FCSTD DOCUMENT  (FreeCAD 0.18R4 (GitTag))
Label: butelka tył
License: All rights reserved
LicenseURL: http://en.wikipedia.org/wiki/All_rights_reserved
objects: Sketcher::SketchObject×1, PartDesign::Body×1
note: 2 computed .brp shape members not serialized (recipe doc carries the construction recipe); baked Part::Feature solids carry a one-line shape summary decoded from their .brp

FEATURE [Sketcher::SketchObject] Sketch
  MapMode = 5
  Support = -> [XY_Plane]
  sketch-geometry (308):
    g0: LineSegment StartX=0 StartY=0 StartZ=0 EndX=160 EndY=0 EndZ=0
    g1: LineSegment StartX=160 StartY=0 StartZ=0 EndX=160 EndY=17.5 EndZ=0
    g2: LineSegment StartX=160 StartY=17.5 StartZ=0 EndX=156.35 EndY=17.5 EndZ=0
    g3: LineSegment StartX=156.35 StartY=17.5 StartZ=0 EndX=156.35 EndY=20.5 EndZ=0
    g4: LineSegment StartX=156.35 StartY=20.5 StartZ=0 EndX=160 EndY=20.5 EndZ=0
    g5: LineSegment StartX=160 StartY=20.5 StartZ=0 EndX=160 EndY=23.5 EndZ=0
    g6: LineSegment StartX=160 StartY=23.5 StartZ=0 EndX=156.35 EndY=23.5 EndZ=0
    g7: LineSegment StartX=156.35 StartY=23.5 StartZ=0 EndX=156.35 EndY=26.5 EndZ=0
    g8: LineSegment StartX=156.35 StartY=26.5 StartZ=0 EndX=160 EndY=26.5 EndZ=0
    g9: LineSegment StartX=160 StartY=26.5 StartZ=0 EndX=160 EndY=29.5 EndZ=0
    g10: LineSegment StartX=160 StartY=29.5 StartZ=0 EndX=156.35 EndY=29.5 EndZ=0
    g11: LineSegment StartX=156.35 StartY=29.5 StartZ=0 EndX=156.35 EndY=32.5 EndZ=0
    g12: LineSegment StartX=156.35 StartY=32.5 StartZ=0 EndX=160 EndY=32.5 EndZ=0
    g13: LineSegment StartX=160 StartY=32.5 StartZ=0 EndX=160 EndY=35.5 EndZ=0
    g14: LineSegment StartX=160 StartY=35.5 StartZ=0 EndX=156.35 EndY=35.5 EndZ=0
    g15: LineSegment StartX=156.35 StartY=35.5 StartZ=0 EndX=156.35 EndY=38.5 EndZ=0
    g16: LineSegment StartX=156.35 StartY=38.5 StartZ=0 EndX=160 EndY=38.5 EndZ=0
    g17: LineSegment StartX=160 StartY=38.5 StartZ=0 EndX=160 EndY=41.5 EndZ=0
    g18: LineSegment StartX=160 StartY=41.5 StartZ=0 EndX=156.35 EndY=41.5 EndZ=0
    g19: LineSegment StartX=156.35 StartY=41.5 StartZ=0 EndX=156.35 EndY=44.5 EndZ=0
    g20: LineSegment StartX=156.35 StartY=44.5 StartZ=0 EndX=160 EndY=44.5 EndZ=0
    g21: LineSegment StartX=160 StartY=44.5 StartZ=0 EndX=160 EndY=47.5 EndZ=0
    g22: LineSegment StartX=160 StartY=47.5 StartZ=0 EndX=156.35 EndY=47.5 EndZ=0
    g23: LineSegment StartX=156.35 StartY=47.5 StartZ=0 EndX=156.35 EndY=50.5 EndZ=0
    g24: LineSegment StartX=156.35 StartY=50.5 StartZ=0 EndX=160 EndY=50.5 EndZ=0
    g25: LineSegment StartX=160 StartY=50.5 StartZ=0 EndX=160 EndY=53.5 EndZ=0
    g26: LineSegment StartX=160 StartY=53.5 StartZ=0 EndX=156.35 EndY=53.5 EndZ=0
    g27: LineSegment StartX=156.35 StartY=53.5 StartZ=0 EndX=156.35 EndY=56.5 EndZ=0
    g28: LineSegment StartX=156.35 StartY=56.5 StartZ=0 EndX=160 EndY=56.5 EndZ=0
    g29: LineSegment StartX=160 StartY=56.5 StartZ=0 EndX=160 EndY=59.5 EndZ=0
    g30: LineSegment StartX=160 StartY=59.5 StartZ=0 EndX=156.35 EndY=59.5 EndZ=0
    g31: LineSegment StartX=156.35 StartY=59.5 StartZ=0 EndX=156.35 EndY=62.5 EndZ=0
    g32: LineSegment StartX=156.35 StartY=62.5 StartZ=0 EndX=160 EndY=62.5 EndZ=0
    g33: LineSegment StartX=160 StartY=62.5 StartZ=0 EndX=160 EndY=65.5 EndZ=0
    g34: LineSegment StartX=160 StartY=65.5 StartZ=0 EndX=156.35 EndY=65.5 EndZ=0
    g35: LineSegment StartX=156.35 StartY=65.5 StartZ=0 EndX=156.35 EndY=68.5 EndZ=0
    g36: LineSegment StartX=156.35 StartY=68.5 StartZ=0 EndX=160 EndY=68.5 EndZ=0
    g37: LineSegment StartX=160 StartY=68.5 StartZ=0 EndX=160 EndY=71.5 EndZ=0
    g38: LineSegment StartX=160 StartY=71.5 StartZ=0 EndX=156.35 EndY=71.5 EndZ=0
    g39: LineSegment StartX=156.35 StartY=71.5 StartZ=0 EndX=156.35 EndY=74.5 EndZ=0
    g40: LineSegment StartX=156.35 StartY=74.5 StartZ=0 EndX=160 EndY=74.5 EndZ=0
    g41: LineSegment StartX=160 StartY=74.5 StartZ=0 EndX=160 EndY=77.5 EndZ=0
    g42: LineSegment StartX=160 StartY=77.5 StartZ=0 EndX=156.35 EndY=77.5 EndZ=0
    g43: LineSegment StartX=156.35 StartY=77.5 StartZ=0 EndX=156.35 EndY=80.5 EndZ=0
    g44: LineSegment StartX=156.35 StartY=80.5 StartZ=0 EndX=160 EndY=80.5 EndZ=0
    g45: LineSegment StartX=160 StartY=80.5 StartZ=0 EndX=160 EndY=83.5 EndZ=0
    g46: LineSegment StartX=160 StartY=83.5 StartZ=0 EndX=156.35 EndY=83.5 EndZ=0
    g47: LineSegment StartX=156.35 StartY=83.5 StartZ=0 EndX=156.35 EndY=86.5 EndZ=0
    g48: LineSegment StartX=156.35 StartY=86.5 StartZ=0 EndX=160 EndY=86.5 EndZ=0
    g49: LineSegment StartX=160 StartY=86.5 StartZ=0 EndX=160 EndY=89.5 EndZ=0
    g50: LineSegment StartX=160 StartY=89.5 StartZ=0 EndX=156.35 EndY=89.5 EndZ=0
    g51: LineSegment StartX=156.35 StartY=89.5 StartZ=0 EndX=156.35 EndY=92.5 EndZ=0
    g52: LineSegment StartX=156.35 StartY=92.5 StartZ=0 EndX=160 EndY=92.5 EndZ=0
    g53: LineSegment StartX=160 StartY=92.5 StartZ=0 EndX=160 EndY=95.5 EndZ=0
    g54: LineSegment StartX=160 StartY=95.5 StartZ=0 EndX=156.35 EndY=95.5 EndZ=0
    g55: LineSegment StartX=156.35 StartY=95.5 StartZ=0 EndX=156.35 EndY=98.5 EndZ=0
    g56: LineSegment StartX=156.35 StartY=98.5 StartZ=0 EndX=160 EndY=98.5 EndZ=0
    g57: LineSegment StartX=160 StartY=98.5 StartZ=0 EndX=160 EndY=101.5 EndZ=0
    g58: LineSegment StartX=160 StartY=101.5 StartZ=0 EndX=156.35 EndY=101.5 EndZ=0
    g59: LineSegment StartX=156.35 StartY=101.5 StartZ=0 EndX=156.35 EndY=104.5 EndZ=0
    g60: LineSegment StartX=156.35 StartY=104.5 StartZ=0 EndX=160 EndY=104.5 EndZ=0
    g61: LineSegment StartX=160 StartY=104.5 StartZ=0 EndX=160 EndY=107.5 EndZ=0
    g62: LineSegment StartX=160 StartY=107.5 StartZ=0 EndX=156.35 EndY=107.5 EndZ=0
    g63: LineSegment StartX=156.35 StartY=107.5 StartZ=0 EndX=156.35 EndY=110.5 EndZ=0
    g64: LineSegment StartX=156.35 StartY=110.5 StartZ=0 EndX=160 EndY=110.5 EndZ=0
    g65: LineSegment StartX=160 StartY=110.5 StartZ=0 EndX=160 EndY=113.5 EndZ=0
    g66: LineSegment StartX=160 StartY=113.5 StartZ=0 EndX=156.35 EndY=113.5 EndZ=0
    g67: LineSegment StartX=156.35 StartY=113.5 StartZ=0 EndX=156.35 EndY=116.5 EndZ=0
    g68: LineSegment StartX=156.35 StartY=116.5 StartZ=0 EndX=160 EndY=116.5 EndZ=0
    g69: LineSegment StartX=160 StartY=116.5 StartZ=0 EndX=160 EndY=119.5 EndZ=0
    g70: LineSegment StartX=160 StartY=119.5 StartZ=0 EndX=156.35 EndY=119.5 EndZ=0
    g71: LineSegment StartX=156.35 StartY=119.5 StartZ=0 EndX=156.35 EndY=122.5 EndZ=0
    g72: LineSegment StartX=156.35 StartY=122.5 StartZ=0 EndX=160 EndY=122.5 EndZ=0
    g73: LineSegment StartX=160 StartY=122.5 StartZ=0 EndX=160 EndY=125.5 EndZ=0
    g74: LineSegment StartX=160 StartY=125.5 StartZ=0 EndX=156.35 EndY=125.5 EndZ=0
    g75: LineSegment StartX=156.35 StartY=125.5 StartZ=0 EndX=156.35 EndY=128.5 EndZ=0
    g76: LineSegment StartX=156.35 StartY=128.5 StartZ=0 EndX=160 EndY=128.5 EndZ=0
    g77: LineSegment StartX=160 StartY=128.5 StartZ=0 EndX=160 EndY=131.5 EndZ=0
    g78: LineSegment StartX=160 StartY=131.5 StartZ=0 EndX=156.35 EndY=131.5 EndZ=0
    g79: LineSegment StartX=156.35 StartY=131.5 StartZ=0 EndX=156.35 EndY=134.5 EndZ=0
    g80: LineSegment StartX=156.35 StartY=134.5 StartZ=0 EndX=160 EndY=134.5 EndZ=0
    g81: LineSegment StartX=160 StartY=134.5 StartZ=0 EndX=160 EndY=137.5 EndZ=0
    g82: LineSegment StartX=160 StartY=137.5 StartZ=0 EndX=156.35 EndY=137.5 EndZ=0
    g83: LineSegment StartX=156.35 StartY=137.5 StartZ=0 EndX=156.35 EndY=140.5 EndZ=0
    g84: LineSegment StartX=156.35 StartY=140.5 StartZ=0 EndX=160 EndY=140.5 EndZ=0
    g85: LineSegment StartX=160 StartY=140.5 StartZ=0 EndX=160 EndY=143.5 EndZ=0
    g86: LineSegment StartX=160 StartY=143.5 StartZ=0 EndX=156.35 EndY=143.5 EndZ=0
    g87: LineSegment StartX=156.35 StartY=143.5 StartZ=0 EndX=156.35 EndY=146.5 EndZ=0
    g88: LineSegment StartX=156.35 StartY=146.5 StartZ=0 EndX=160 EndY=146.5 EndZ=0
    g89: LineSegment StartX=160 StartY=146.5 StartZ=0 EndX=160 EndY=149.5 EndZ=0
    g90: LineSegment StartX=160 StartY=149.5 StartZ=0 EndX=156.35 EndY=149.5 EndZ=0
    g91: LineSegment StartX=156.35 StartY=149.5 StartZ=0 EndX=156.35 EndY=152.5 EndZ=0
    g92: LineSegment StartX=156.35 StartY=152.5 StartZ=0 EndX=160 EndY=152.5 EndZ=0
    g93: LineSegment StartX=160 StartY=152.5 StartZ=0 EndX=160 EndY=155.5 EndZ=0
    g94: LineSegment StartX=160 StartY=155.5 StartZ=0 EndX=156.35 EndY=155.5 EndZ=0
    g95: LineSegment StartX=156.35 StartY=155.5 StartZ=0 EndX=156.35 EndY=158.5 EndZ=0
    g96: LineSegment StartX=156.35 StartY=158.5 StartZ=0 EndX=160 EndY=158.5 EndZ=0
    g97: LineSegment StartX=160 StartY=158.5 StartZ=0 EndX=160 EndY=161.5 EndZ=0
    g98: LineSegment StartX=160 StartY=161.5 StartZ=0 EndX=156.35 EndY=161.5 EndZ=0
    g99: LineSegment StartX=156.35 StartY=161.5 StartZ=0 EndX=156.35 EndY=164.5 EndZ=0
    g100: LineSegment StartX=156.35 StartY=164.5 StartZ=0 EndX=160 EndY=164.5 EndZ=0
    g101: LineSegment StartX=160 StartY=164.5 StartZ=0 EndX=160 EndY=167.5 EndZ=0
    g102: LineSegment StartX=160 StartY=167.5 StartZ=0 EndX=156.35 EndY=167.5 EndZ=0
    g103: LineSegment StartX=156.35 StartY=167.5 StartZ=0 EndX=156.35 EndY=170.5 EndZ=0
    g104: LineSegment StartX=156.35 StartY=170.5 StartZ=0 EndX=160 EndY=170.5 EndZ=0
    g105: LineSegment StartX=160 StartY=170.5 StartZ=0 EndX=160 EndY=173.5 EndZ=0
    g106: LineSegment StartX=160 StartY=173.5 StartZ=0 EndX=156.35 EndY=173.5 EndZ=0
    g107: LineSegment StartX=156.35 StartY=173.5 StartZ=0 EndX=156.35 EndY=176.5 EndZ=0
    g108: LineSegment StartX=156.35 StartY=176.5 StartZ=0 EndX=160 EndY=176.5 EndZ=0
    g109: LineSegment StartX=160 StartY=176.5 StartZ=0 EndX=160 EndY=179.5 EndZ=0
    g110: LineSegment StartX=160 StartY=179.5 StartZ=0 EndX=156.35 EndY=179.5 EndZ=0
    g111: LineSegment StartX=156.35 StartY=179.5 StartZ=0 EndX=156.35 EndY=182.5 EndZ=0
    g112: LineSegment StartX=156.35 StartY=182.5 StartZ=0 EndX=160 EndY=182.5 EndZ=0
    g113: LineSegment StartX=160 StartY=182.5 StartZ=0 EndX=160 EndY=185.5 EndZ=0
    g114: LineSegment StartX=160 StartY=185.5 StartZ=0 EndX=156.35 EndY=185.5 EndZ=0
    g115: LineSegment StartX=156.35 StartY=185.5 StartZ=0 EndX=156.35 EndY=188.5 EndZ=0
    g116: LineSegment StartX=156.35 StartY=188.5 StartZ=0 EndX=160 EndY=188.5 EndZ=0
    g117: LineSegment StartX=160 StartY=188.5 StartZ=0 EndX=160 EndY=191.5 EndZ=0
    g118: LineSegment StartX=160 StartY=191.5 StartZ=0 EndX=156.35 EndY=191.5 EndZ=0
    g119: LineSegment StartX=156.35 StartY=191.5 StartZ=0 EndX=156.35 EndY=194.5 EndZ=0
    g120: LineSegment StartX=156.35 StartY=194.5 StartZ=0 EndX=160 EndY=194.5 EndZ=0
    g121: LineSegment StartX=160 StartY=194.5 StartZ=0 EndX=160 EndY=197.5 EndZ=0
    g122: LineSegment StartX=160 StartY=197.5 StartZ=0 EndX=156.35 EndY=197.5 EndZ=0
    g123: LineSegment StartX=156.35 StartY=197.5 StartZ=0 EndX=156.35 EndY=200.5 EndZ=0
    g124: LineSegment StartX=156.35 StartY=200.5 StartZ=0 EndX=160 EndY=200.5 EndZ=0
    g125: LineSegment StartX=160 StartY=200.5 StartZ=0 EndX=160 EndY=203.5 EndZ=0
    g126: LineSegment StartX=160 StartY=203.5 StartZ=0 EndX=156.35 EndY=203.5 EndZ=0
    g127: LineSegment StartX=156.35 StartY=203.5 StartZ=0 EndX=156.35 EndY=206.5 EndZ=0
    g128: LineSegment StartX=156.35 StartY=206.5 StartZ=0 EndX=160 EndY=206.5 EndZ=0
    g129: LineSegment StartX=160 StartY=206.5 StartZ=0 EndX=160 EndY=209.5 EndZ=0
    g130: LineSegment StartX=160 StartY=209.5 StartZ=0 EndX=156.35 EndY=209.5 EndZ=0
    g131: LineSegment StartX=156.35 StartY=209.5 StartZ=0 EndX=156.35 EndY=212.5 EndZ=0
    g132: LineSegment StartX=156.35 StartY=212.5 StartZ=0 EndX=160 EndY=212.5 EndZ=0
    g133: LineSegment StartX=160 StartY=212.5 StartZ=0 EndX=160 EndY=215.5 EndZ=0
    g134: LineSegment StartX=160 StartY=215.5 StartZ=0 EndX=156.35 EndY=215.5 EndZ=0
    g135: LineSegment StartX=156.35 StartY=215.5 StartZ=0 EndX=156.35 EndY=218.5 EndZ=0
    g136: LineSegment StartX=156.35 StartY=218.5 StartZ=0 EndX=160 EndY=218.5 EndZ=0
    g137: LineSegment StartX=160 StartY=218.5 StartZ=0 EndX=160 EndY=221.5 EndZ=0
    g138: LineSegment StartX=160 StartY=221.5 StartZ=0 EndX=156.35 EndY=221.5 EndZ=0
    g139: LineSegment StartX=156.35 StartY=221.5 StartZ=0 EndX=156.35 EndY=224.5 EndZ=0
    g140: LineSegment StartX=156.35 StartY=224.5 StartZ=0 EndX=160 EndY=224.5 EndZ=0
    g141: LineSegment StartX=160 StartY=224.5 StartZ=0 EndX=160 EndY=227.5 EndZ=0
    g142: LineSegment StartX=160 StartY=227.5 StartZ=0 EndX=156.35 EndY=227.5 EndZ=0
    g143: LineSegment StartX=156.35 StartY=227.5 StartZ=0 EndX=156.35 EndY=230.5 EndZ=0
    g144: LineSegment StartX=156.35 StartY=230.5 StartZ=0 EndX=160 EndY=230.5 EndZ=0
    g145: LineSegment StartX=160 StartY=230.5 StartZ=0 EndX=160 EndY=233.5 EndZ=0
    g146: LineSegment StartX=160 StartY=233.5 StartZ=0 EndX=156.35 EndY=233.5 EndZ=0
    g147: LineSegment StartX=156.35 StartY=233.5 StartZ=0 EndX=156.35 EndY=236.5 EndZ=0
    g148: LineSegment StartX=156.35 StartY=236.5 StartZ=0 EndX=160 EndY=236.5 EndZ=0
    g149: LineSegment StartX=160 StartY=236.5 StartZ=0 EndX=160 EndY=239.5 EndZ=0
    g150: LineSegment StartX=160 StartY=239.5 StartZ=0 EndX=156.35 EndY=239.5 EndZ=0
    g151: LineSegment StartX=156.35 StartY=239.5 StartZ=0 EndX=156.35 EndY=242.5 EndZ=0
    g152: LineSegment StartX=156.35 StartY=242.5 StartZ=0 EndX=160 EndY=242.5 EndZ=0
    g153: LineSegment StartX=160 StartY=242.5 StartZ=0 EndX=160 EndY=260 EndZ=0
    g154: LineSegment StartX=160 StartY=260 StartZ=0 EndX=0 EndY=260 EndZ=0
    g155: LineSegment StartX=0 StartY=260 StartZ=0 EndX=0 EndY=242.5 EndZ=0
    g156: LineSegment StartX=0 StartY=242.5 StartZ=0 EndX=3.65 EndY=242.5 EndZ=0
    g157: LineSegment StartX=3.65 StartY=242.5 StartZ=0 EndX=3.65 EndY=239.5 EndZ=0
    g158: LineSegment StartX=3.65 StartY=239.5 StartZ=0 EndX=0 EndY=239.5 EndZ=0
    g159: LineSegment StartX=0 StartY=239.5 StartZ=0 EndX=0 EndY=236.5 EndZ=0
    g160: LineSegment StartX=0 StartY=236.5 StartZ=0 EndX=3.65 EndY=236.5 EndZ=0
    g161: LineSegment StartX=3.65 StartY=236.5 StartZ=0 EndX=3.65 EndY=233.5 EndZ=0
    g162: LineSegment StartX=3.65 StartY=233.5 StartZ=0 EndX=0 EndY=233.5 EndZ=0
    g163: LineSegment StartX=0 StartY=233.5 StartZ=0 EndX=0 EndY=230.5 EndZ=0
    g164: LineSegment StartX=0 StartY=230.5 StartZ=0 EndX=3.65 EndY=230.5 EndZ=0
    g165: LineSegment StartX=3.65 StartY=230.5 StartZ=0 EndX=3.65 EndY=227.5 EndZ=0
    g166: LineSegment StartX=3.65 StartY=227.5 StartZ=0 EndX=0 EndY=227.5 EndZ=0
    g167: LineSegment StartX=0 StartY=227.5 StartZ=0 EndX=0 EndY=224.5 EndZ=0
    g168: LineSegment StartX=0 StartY=224.5 StartZ=0 EndX=3.65 EndY=224.5 EndZ=0
    g169: LineSegment StartX=3.65 StartY=224.5 StartZ=0 EndX=3.65 EndY=221.5 EndZ=0
    g170: LineSegment StartX=3.65 StartY=221.5 StartZ=0 EndX=0 EndY=221.5 EndZ=0
    g171: LineSegment StartX=0 StartY=221.5 StartZ=0 EndX=0 EndY=218.5 EndZ=0
    g172: LineSegment StartX=0 StartY=218.5 StartZ=0 EndX=3.65 EndY=218.5 EndZ=0
    g173: LineSegment StartX=3.65 StartY=218.5 StartZ=0 EndX=3.65 EndY=215.5 EndZ=0
    g174: LineSegment StartX=3.65 StartY=215.5 StartZ=0 EndX=0 EndY=215.5 EndZ=0
    g175: LineSegment StartX=0 StartY=215.5 StartZ=0 EndX=0 EndY=212.5 EndZ=0
    g176: LineSegment StartX=0 StartY=212.5 StartZ=0 EndX=3.65 EndY=212.5 EndZ=0
    g177: LineSegment StartX=3.65 StartY=212.5 StartZ=0 EndX=3.65 EndY=209.5 EndZ=0
    g178: LineSegment StartX=3.65 StartY=209.5 StartZ=0 EndX=0 EndY=209.5 EndZ=0
    g179: LineSegment StartX=0 StartY=209.5 StartZ=0 EndX=0 EndY=206.5 EndZ=0
    g180: LineSegment StartX=0 StartY=206.5 StartZ=0 EndX=3.65 EndY=206.5 EndZ=0
    g181: LineSegment StartX=3.65 StartY=206.5 StartZ=0 EndX=3.65 EndY=203.5 EndZ=0
    g182: LineSegment StartX=3.65 StartY=203.5 StartZ=0 EndX=0 EndY=203.5 EndZ=0
    g183: LineSegment StartX=0 StartY=203.5 StartZ=0 EndX=0 EndY=200.5 EndZ=0
    g184: LineSegment StartX=0 StartY=200.5 StartZ=0 EndX=3.65 EndY=200.5 EndZ=0
    g185: LineSegment StartX=3.65 StartY=200.5 StartZ=0 EndX=3.65 EndY=197.5 EndZ=0
    g186: LineSegment StartX=3.65 StartY=197.5 StartZ=0 EndX=0 EndY=197.5 EndZ=0
    g187: LineSegment StartX=0 StartY=197.5 StartZ=0 EndX=0 EndY=194.5 EndZ=0
    g188: LineSegment StartX=0 StartY=194.5 StartZ=0 EndX=3.65 EndY=194.5 EndZ=0
    g189: LineSegment StartX=3.65 StartY=194.5 StartZ=0 EndX=3.65 EndY=191.5 EndZ=0
    g190: LineSegment StartX=3.65 StartY=191.5 StartZ=0 EndX=0 EndY=191.5 EndZ=0
    g191: LineSegment StartX=0 StartY=191.5 StartZ=0 EndX=0 EndY=188.5 EndZ=0
    g192: LineSegment StartX=0 StartY=188.5 StartZ=0 EndX=3.65 EndY=188.5 EndZ=0
    g193: LineSegment StartX=3.65 StartY=188.5 StartZ=0 EndX=3.65 EndY=185.5 EndZ=0
    g194: LineSegment StartX=3.65 StartY=185.5 StartZ=0 EndX=0 EndY=185.5 EndZ=0
    g195: LineSegment StartX=0 StartY=185.5 StartZ=0 EndX=0 EndY=182.5 EndZ=0
    g196: LineSegment StartX=0 StartY=182.5 StartZ=0 EndX=3.65 EndY=182.5 EndZ=0
    g197: LineSegment StartX=3.65 StartY=182.5 StartZ=0 EndX=3.65 EndY=179.5 EndZ=0
    g198: LineSegment StartX=3.65 StartY=179.5 StartZ=0 EndX=0 EndY=179.5 EndZ=0
    g199: LineSegment StartX=0 StartY=179.5 StartZ=0 EndX=0 EndY=176.5 EndZ=0
    g200: LineSegment StartX=0 StartY=176.5 StartZ=0 EndX=3.65 EndY=176.5 EndZ=0
    g201: LineSegment StartX=3.65 StartY=176.5 StartZ=0 EndX=3.65 EndY=173.5 EndZ=0
    g202: LineSegment StartX=3.65 StartY=173.5 StartZ=0 EndX=0 EndY=173.5 EndZ=0
    g203: LineSegment StartX=0 StartY=173.5 StartZ=0 EndX=0 EndY=170.5 EndZ=0
    g204: LineSegment StartX=0 StartY=170.5 StartZ=0 EndX=3.65 EndY=170.5 EndZ=0
    g205: LineSegment StartX=3.65 StartY=170.5 StartZ=0 EndX=3.65 EndY=167.5 EndZ=0
    g206: LineSegment StartX=3.65 StartY=167.5 StartZ=0 EndX=0 EndY=167.5 EndZ=0
    g207: LineSegment StartX=0 StartY=167.5 StartZ=0 EndX=0 EndY=164.5 EndZ=0
    g208: LineSegment StartX=0 StartY=164.5 StartZ=0 EndX=3.65 EndY=164.5 EndZ=0
    g209: LineSegment StartX=3.65 StartY=164.5 StartZ=0 EndX=3.65 EndY=161.5 EndZ=0
    g210: LineSegment StartX=3.65 StartY=161.5 StartZ=0 EndX=0 EndY=161.5 EndZ=0
    g211: LineSegment StartX=0 StartY=161.5 StartZ=0 EndX=0 EndY=158.5 EndZ=0
    g212: LineSegment StartX=0 StartY=158.5 StartZ=0 EndX=3.65 EndY=158.5 EndZ=0
    g213: LineSegment StartX=3.65 StartY=158.5 StartZ=0 EndX=3.65 EndY=155.5 EndZ=0
    g214: LineSegment StartX=3.65 StartY=155.5 StartZ=0 EndX=0 EndY=155.5 EndZ=0
    g215: LineSegment StartX=0 StartY=155.5 StartZ=0 EndX=0 EndY=152.5 EndZ=0
    g216: LineSegment StartX=0 StartY=152.5 StartZ=0 EndX=3.65 EndY=152.5 EndZ=0
    g217: LineSegment StartX=3.65 StartY=152.5 StartZ=0 EndX=3.65 EndY=149.5 EndZ=0
    g218: LineSegment StartX=3.65 StartY=149.5 StartZ=0 EndX=0 EndY=149.5 EndZ=0
    g219: LineSegment StartX=0 StartY=149.5 StartZ=0 EndX=0 EndY=146.5 EndZ=0
    g220: LineSegment StartX=0 StartY=146.5 StartZ=0 EndX=3.65 EndY=146.5 EndZ=0
    g221: LineSegment StartX=3.65 StartY=146.5 StartZ=0 EndX=3.65 EndY=143.5 EndZ=0
    g222: LineSegment StartX=3.65 StartY=143.5 StartZ=0 EndX=0 EndY=143.5 EndZ=0
    g223: LineSegment StartX=0 StartY=143.5 StartZ=0 EndX=0 EndY=140.5 EndZ=0
    g224: LineSegment StartX=0 StartY=140.5 StartZ=0 EndX=3.65 EndY=140.5 EndZ=0
    g225: LineSegment StartX=3.65 StartY=140.5 StartZ=0 EndX=3.65 EndY=137.5 EndZ=0
    g226: LineSegment StartX=3.65 StartY=137.5 StartZ=0 EndX=0 EndY=137.5 EndZ=0
    g227: LineSegment StartX=0 StartY=137.5 StartZ=0 EndX=0 EndY=134.5 EndZ=0
    g228: LineSegment StartX=0 StartY=134.5 StartZ=0 EndX=3.65 EndY=134.5 EndZ=0
    g229: LineSegment StartX=3.65 StartY=134.5 StartZ=0 EndX=3.65 EndY=131.5 EndZ=0
    g230: LineSegment StartX=3.65 StartY=131.5 StartZ=0 EndX=0 EndY=131.5 EndZ=0
    g231: LineSegment StartX=0 StartY=131.5 StartZ=0 EndX=0 EndY=128.5 EndZ=0
    g232: LineSegment StartX=0 StartY=128.5 StartZ=0 EndX=3.65 EndY=128.5 EndZ=0
    g233: LineSegment StartX=3.65 StartY=128.5 StartZ=0 EndX=3.65 EndY=125.5 EndZ=0
    g234: LineSegment StartX=3.65 StartY=125.5 StartZ=0 EndX=0 EndY=125.5 EndZ=0
    g235: LineSegment StartX=0 StartY=125.5 StartZ=0 EndX=0 EndY=122.5 EndZ=0
    g236: LineSegment StartX=0 StartY=122.5 StartZ=0 EndX=3.65 EndY=122.5 EndZ=0
    g237: LineSegment StartX=3.65 StartY=122.5 StartZ=0 EndX=3.65 EndY=119.5 EndZ=0
    g238: LineSegment StartX=3.65 StartY=119.5 StartZ=0 EndX=0 EndY=119.5 EndZ=0
    g239: LineSegment StartX=0 StartY=119.5 StartZ=0 EndX=0 EndY=116.5 EndZ=0
    g240: LineSegment StartX=0 StartY=116.5 StartZ=0 EndX=3.65 EndY=116.5 EndZ=0
    g241: LineSegment StartX=3.65 StartY=116.5 StartZ=0 EndX=3.65 EndY=113.5 EndZ=0
    g242: LineSegment StartX=3.65 StartY=113.5 StartZ=0 EndX=0 EndY=113.5 EndZ=0
    g243: LineSegment StartX=0 StartY=113.5 StartZ=0 EndX=0 EndY=110.5 EndZ=0
    g244: LineSegment StartX=0 StartY=110.5 StartZ=0 EndX=3.65 EndY=110.5 EndZ=0
    g245: LineSegment StartX=3.65 StartY=110.5 StartZ=0 EndX=3.65 EndY=107.5 EndZ=0
    g246: LineSegment StartX=3.65 StartY=107.5 StartZ=0 EndX=0 EndY=107.5 EndZ=0
    g247: LineSegment StartX=0 StartY=107.5 StartZ=0 EndX=0 EndY=104.5 EndZ=0
    g248: LineSegment StartX=0 StartY=104.5 StartZ=0 EndX=3.65 EndY=104.5 EndZ=0
    g249: LineSegment StartX=3.65 StartY=104.5 StartZ=0 EndX=3.65 EndY=101.5 EndZ=0
    g250: LineSegment StartX=3.65 StartY=101.5 StartZ=0 EndX=0 EndY=101.5 EndZ=0
    g251: LineSegment StartX=0 StartY=101.5 StartZ=0 EndX=0 EndY=98.5 EndZ=0
    g252: LineSegment StartX=0 StartY=98.5 StartZ=0 EndX=3.65 EndY=98.5 EndZ=0
    g253: LineSegment StartX=3.65 StartY=98.5 StartZ=0 EndX=3.65 EndY=95.5 EndZ=0
    g254: LineSegment StartX=3.65 StartY=95.5 StartZ=0 EndX=0 EndY=95.5 EndZ=0
    g255: LineSegment StartX=0 StartY=95.5 StartZ=0 EndX=0 EndY=92.5 EndZ=0
    g256: LineSegment StartX=0 StartY=92.5 StartZ=0 EndX=3.65 EndY=92.5 EndZ=0
    g257: LineSegment StartX=3.65 StartY=92.5 StartZ=0 EndX=3.65 EndY=89.5 EndZ=0
    g258: LineSegment StartX=3.65 StartY=89.5 StartZ=0 EndX=0 EndY=89.5 EndZ=0
    g259: LineSegment StartX=0 StartY=89.5 StartZ=0 EndX=0 EndY=86.5 EndZ=0
    g260: LineSegment StartX=0 StartY=86.5 StartZ=0 EndX=3.65 EndY=86.5 EndZ=0
    g261: LineSegment StartX=3.65 StartY=86.5 StartZ=0 EndX=3.65 EndY=83.5 EndZ=0
    g262: LineSegment StartX=3.65 StartY=83.5 StartZ=0 EndX=0 EndY=83.5 EndZ=0
    g263: LineSegment StartX=0 StartY=83.5 StartZ=0 EndX=0 EndY=80.5 EndZ=0
    g264: LineSegment StartX=0 StartY=80.5 StartZ=0 EndX=3.65 EndY=80.5 EndZ=0
    g265: LineSegment StartX=3.65 StartY=80.5 StartZ=0 EndX=3.65 EndY=77.5 EndZ=0
    g266: LineSegment StartX=3.65 StartY=77.5 StartZ=0 EndX=0 EndY=77.5 EndZ=0
    g267: LineSegment StartX=0 StartY=77.5 StartZ=0 EndX=0 EndY=74.5 EndZ=0
    g268: LineSegment StartX=0 StartY=74.5 StartZ=0 EndX=3.65 EndY=74.5 EndZ=0
    g269: LineSegment StartX=3.65 StartY=74.5 StartZ=0 EndX=3.65 EndY=71.5 EndZ=0
    g270: LineSegment StartX=3.65 StartY=71.5 StartZ=0 EndX=0 EndY=71.5 EndZ=0
    g271: LineSegment StartX=0 StartY=71.5 StartZ=0 EndX=0 EndY=68.5 EndZ=0
    g272: LineSegment StartX=0 StartY=68.5 StartZ=0 EndX=3.65 EndY=68.5 EndZ=0
    g273: LineSegment StartX=3.65 StartY=68.5 StartZ=0 EndX=3.65 EndY=65.5 EndZ=0
    g274: LineSegment StartX=3.65 StartY=65.5 StartZ=0 EndX=0 EndY=65.5 EndZ=0
    g275: LineSegment StartX=0 StartY=65.5 StartZ=0 EndX=0 EndY=62.5 EndZ=0
    g276: LineSegment StartX=0 StartY=62.5 StartZ=0 EndX=3.65 EndY=62.5 EndZ=0
    g277: LineSegment StartX=3.65 StartY=62.5 StartZ=0 EndX=3.65 EndY=59.5 EndZ=0
    g278: LineSegment StartX=3.65 StartY=59.5 StartZ=0 EndX=0 EndY=59.5 EndZ=0
    g279: LineSegment StartX=0 StartY=59.5 StartZ=0 EndX=0 EndY=56.5 EndZ=0
    g280: LineSegment StartX=0 StartY=56.5 StartZ=0 EndX=3.65 EndY=56.5 EndZ=0
    g281: LineSegment StartX=3.65 StartY=56.5 StartZ=0 EndX=3.65 EndY=53.5 EndZ=0
    g282: LineSegment StartX=3.65 StartY=53.5 StartZ=0 EndX=0 EndY=53.5 EndZ=0
    g283: LineSegment StartX=0 StartY=53.5 StartZ=0 EndX=0 EndY=50.5 EndZ=0
    g284: LineSegment StartX=0 StartY=50.5 StartZ=0 EndX=3.65 EndY=50.5 EndZ=0
    g285: LineSegment StartX=3.65 StartY=50.5 StartZ=0 EndX=3.65 EndY=47.5 EndZ=0
    g286: LineSegment StartX=3.65 StartY=47.5 StartZ=0 EndX=0 EndY=47.5 EndZ=0
    g287: LineSegment StartX=0 StartY=47.5 StartZ=0 EndX=0 EndY=44.5 EndZ=0
    g288: LineSegment StartX=0 StartY=44.5 StartZ=0 EndX=3.65 EndY=44.5 EndZ=0
    g289: LineSegment StartX=3.65 StartY=44.5 StartZ=0 EndX=3.65 EndY=41.5 EndZ=0
    g290: LineSegment StartX=3.65 StartY=41.5 StartZ=0 EndX=0 EndY=41.5 EndZ=0
    g291: LineSegment StartX=0 StartY=41.5 StartZ=0 EndX=0 EndY=38.5 EndZ=0
    g292: LineSegment StartX=0 StartY=38.5 StartZ=0 EndX=3.65 EndY=38.5 EndZ=0
    g293: LineSegment StartX=3.65 StartY=38.5 StartZ=0 EndX=3.65 EndY=35.5 EndZ=0
    g294: LineSegment StartX=3.65 StartY=35.5 StartZ=0 EndX=0 EndY=35.5 EndZ=0
    g295: LineSegment StartX=0 StartY=35.5 StartZ=0 EndX=0 EndY=32.5 EndZ=0
    g296: LineSegment StartX=0 StartY=32.5 StartZ=0 EndX=3.65 EndY=32.5 EndZ=0
    g297: LineSegment StartX=3.65 StartY=32.5 StartZ=0 EndX=3.65 EndY=29.5 EndZ=0
    g298: LineSegment StartX=3.65 StartY=29.5 StartZ=0 EndX=0 EndY=29.5 EndZ=0
    g299: LineSegment StartX=0 StartY=29.5 StartZ=0 EndX=0 EndY=26.5 EndZ=0
    g300: LineSegment StartX=0 StartY=26.5 StartZ=0 EndX=3.65 EndY=26.5 EndZ=0
    g301: LineSegment StartX=3.65 StartY=26.5 StartZ=0 EndX=3.65 EndY=23.5 EndZ=0
    g302: LineSegment StartX=3.65 StartY=23.5 StartZ=0 EndX=0 EndY=23.5 EndZ=0
    g303: LineSegment StartX=0 StartY=23.5 StartZ=0 EndX=0 EndY=20.5 EndZ=0
    g304: LineSegment StartX=0 StartY=20.5 StartZ=0 EndX=3.65 EndY=20.5 EndZ=0
    g305: LineSegment StartX=3.65 StartY=20.5 StartZ=0 EndX=3.65 EndY=17.5 EndZ=0
    g306: LineSegment StartX=3.65 StartY=17.5 StartZ=0 EndX=0 EndY=17.5 EndZ=0
    g307: LineSegment StartX=0 StartY=17.5 StartZ=0 EndX=0 EndY=0 EndZ=0
FEATURE [PartDesign::Body] Body
  Group = -> [Sketch]
  Origin = -> Origin
